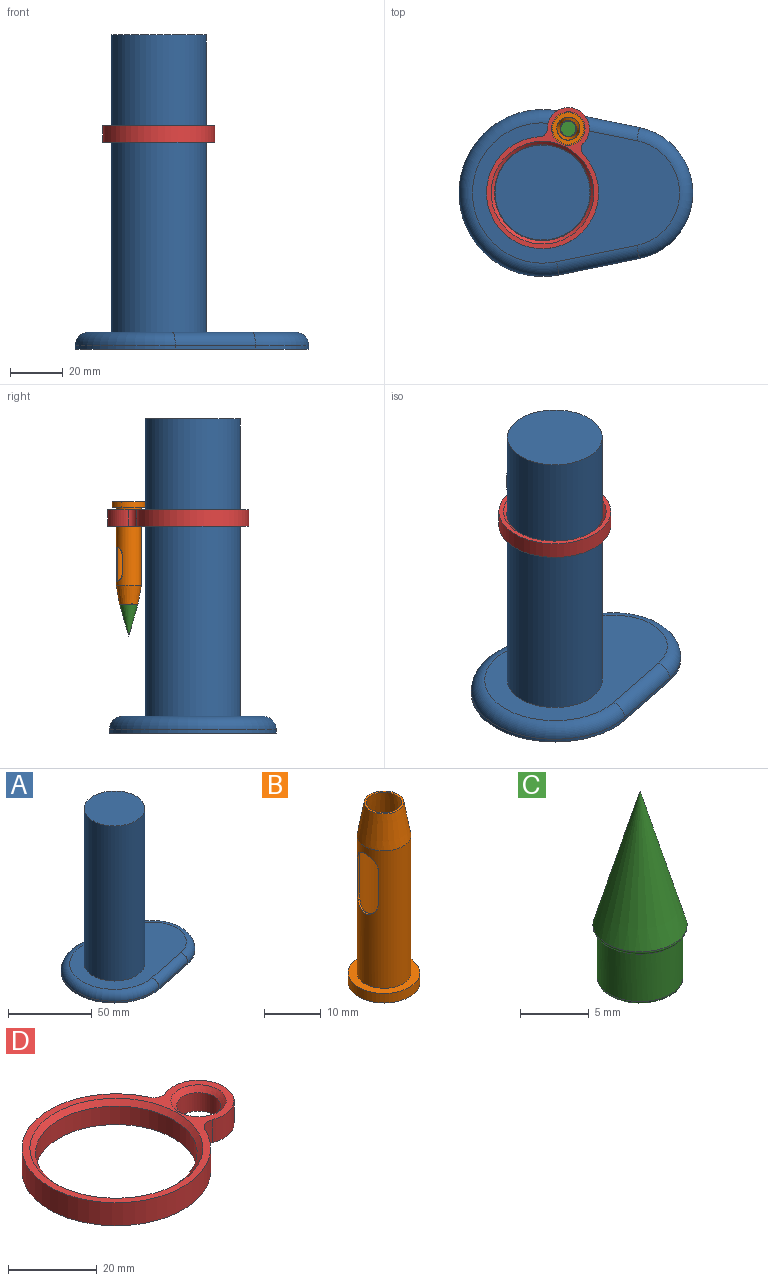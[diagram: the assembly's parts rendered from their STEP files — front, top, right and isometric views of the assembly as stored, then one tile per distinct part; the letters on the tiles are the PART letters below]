
ASSEMBLY  parts=4 mates=3
PART A: 21 faces, bbox 93.6x68.7x119.4 mm
  f0: plane 88.9x63.5mm, normal (0,0,-1), area 600.3mm2, adj f1,f2,f3,f4,f10,f11,f12,f13
  f1: plane 30.48x6.22mm, normal (0.2,0.98,0), area 39.5mm2, adj f0,f2,f4,f8
  f2: cylinder r=31.75mm len=63.5mm, axis (0,0,-1), area 142.9mm2, adj f0,f1,f3,f6
  f3: plane 30.48x6.22mm, normal (0.2,-0.98,0), area 39.5mm2, adj f0,f2,f4,f7
  f4: cylinder r=25.4mm len=49.77mm, axis (0,0,-1), area 88.4mm2, adj f0,f1,f3,f9
  f5: plane 78.74x53.34mm, normal (0,0,1), area 2263.3mm2, adj f6,f7,f8,f9,f19
  f6: torus R=26.67mm, axis (0,0,1), area 845.8mm2, adj f2,f5,f7,f8
  f7: cylinder r=5.08mm len=31.5mm, axis (-0.98,-0.2,0), area 248.2mm2, adj f3,f5,f6,f9
  f8: cylinder r=5.08mm len=31.5mm, axis (0.98,-0.2,0), area 248.2mm2, adj f1,f5,f6,f9
  f9: torus R=20.32mm, axis (0,0,1), area 514.8mm2, adj f4,f5,f7,f8
  f10: plane 30.48x6.22mm, normal (-0.2,-0.98,0), area 39.5mm2, adj f0,f11,f13,f17
  f11: cylinder r=29.21mm len=58.42mm, axis (0,0,-1), area 131.5mm2, adj f0,f10,f12,f15
  f12: plane 30.48x6.22mm, normal (-0.2,0.98,0), area 39.5mm2, adj f0,f11,f13,f16
  f13: cylinder r=22.86mm len=44.8mm, axis (0,0,-1), area 79.5mm2, adj f0,f10,f12,f18
  f14: plane 78.74x53.34mm, normal (0,0,-1), area 3287.7mm2, adj f15,f16,f17,f18
  f15: torus R=26.67mm, axis (0,0,1), area 400mm2, adj f11,f14,f16,f17
  f16: cylinder r=2.54mm len=30.99mm, axis (-0.98,-0.2,0), area 124.1mm2, adj f12,f14,f15,f18
  f17: cylinder r=2.54mm len=30.99mm, axis (0.98,-0.2,0), area 124.1mm2, adj f10,f14,f15,f18
  f18: torus R=20.32mm, axis (0,0,1), area 239.7mm2, adj f13,f14,f16,f17
  f19: cylinder r=18.06mm len=113.03mm, axis (0,0,-1), area 12824.4mm2, adj f5,f20
  f20: plane 36.12x36.12mm, normal (0,0,1), area 1024.4mm2, adj f19
PART B: 20 faces, bbox 12.7x12.7x38.9 mm
  f0: cylinder r=4.76mm len=29.72mm, axis (0,0,-1), area 763.6mm2, adj f3,f5,f11,f12,f13,f14,f15,f16
  f1: cylinder r=4.38mm len=30.07mm, axis (0,0,-1), area 700.7mm2, adj f8,f10,f11,f12,f13,f14,f15,f16
  f2: cylinder r=6.35mm len=12.7mm, axis (0,0,-1), area 82.1mm2, adj f3,f4
  f3: plane 12.7x12.7mm, normal (0,0,1), area 55.4mm2, adj f0,f2
  f4: plane 12.7x12.7mm, normal (0,0,-1), area 66.4mm2, adj f2,f19
  f5: cone r=4.76mm half-angle=10deg, axis (0,0,-1), area 187.6mm2, adj f0,f6
  f6: plane 7.02x7.02mm, normal (0,0,1), area 8.1mm2, adj f5,f10
  f7: cylinder r=5.97mm len=11.94mm, axis (0,0,-1), area 48.6mm2, adj f8,f9
  f8: plane 11.94x11.94mm, normal (0,0,-1), area 51.6mm2, adj f1,f7
  f9: plane 11.94x11.94mm, normal (0,0,1), area 51.6mm2, adj f7,f19
  f10: cone r=4.39mm half-angle=10deg, axis (0,0,-1), area 171mm2, adj f1,f6
  f11: plane 7.8x0.46mm, normal (0,-1,0), area 3.6mm2, adj f0,f1,f12,f14
  f12: cylinder r=2.54mm len=5.08mm, axis (-1,0,0), area 3.3mm2, adj f0,f1,f11,f13
  f13: plane 7.8x0.46mm, normal (0,1,0), area 3.6mm2, adj f0,f1,f12,f14
  f14: cylinder r=2.54mm len=5.08mm, axis (-1,0,0), area 3.3mm2, adj f0,f1,f11,f13
  f15: cylinder r=2.54mm len=5.08mm, axis (-1,0,0), area 3.3mm2, adj f0,f1,f16,f18
  f16: plane 7.8x0.46mm, normal (0,1,0), area 3.6mm2, adj f0,f1,f15,f17
  f17: cylinder r=2.54mm len=5.08mm, axis (-1,0,0), area 3.3mm2, adj f0,f1,f16,f18
  f18: plane 7.8x0.46mm, normal (0,-1,0), area 3.6mm2, adj f0,f1,f15,f17
  f19: cylinder r=4.38mm len=8.76mm, axis (0,0,-1), area 10.5mm2, adj f4,f9
PART C: 6 faces, bbox 7.4x7.4x16.8 mm
  f0: cone r=3.51mm half-angle=16deg, axis (0,0,-1), area 133mm2, adj f5
  f1: plane 6.34x6.34mm, normal (0,0,-1), area 1mm2, adj f2,f5
  f2: cylinder r=3.12mm len=6.24mm, axis (0,0,1), area 84.7mm2, adj f1,f4
  f3: plane 5.74x5.74mm, normal (0,0,-1), area 25.8mm2, adj f4
  f4: torus R=2.87mm, axis (0,0,-1), area 7.6mm2, adj f2,f3
  f5: torus R=3.17mm, axis (0,0,1), area 9.9mm2, adj f0,f1
PART D: 10 faces, bbox 55.6x42.6x6.4 mm
  f0: cylinder r=3.05mm len=6.35mm, axis (0,0,-1), area 29.5mm2, adj f1,f4,f6,f7
  f1: cylinder r=8.01mm len=16.02mm, axis (0,0,-1), area 199.1mm2, adj f0,f2,f6,f7
  f2: cylinder r=3.05mm len=6.35mm, axis (0,0,-1), area 29.5mm2, adj f1,f4,f6,f7
  f3: cylinder r=18.26mm len=36.51mm, axis (0,0,-1), area 582.7mm2, adj f7,f9
  f4: cylinder r=21.3mm len=42.61mm, axis (0,0,-1), area 732.6mm2, adj f0,f2,f6,f7
  f5: cylinder r=4.96mm len=9.92mm, axis (0,0,-1), area 158.3mm2, adj f7,f8
  f6: plane 55.58x42.61mm, normal (0,0,1), area 289.5mm2, adj f0,f1,f2,f4,f8,f9
  f7: plane 55.58x42.61mm, normal (0,0,-1), area 484.9mm2, adj f0,f1,f2,f3,f4,f5
  f8: cone r=4.96mm half-angle=45deg, axis (0,0,1), area 63.1mm2, adj f5,f6
  f9: cone r=18.26mm half-angle=45deg, axis (0,0,1), area 213.2mm2, adj f3,f6
PLACE A t=(-36.45,17.25,-16.63)mm fixed
PLACE B rot(axis=(0.84,-0.54,0),180deg) t=(-26.64,41.62,71.24)mm
PLACE C rot(axis=(0.84,-0.54,0),180deg) t=(-26.64,41.62,71.34)mm
PLACE D rot(axis=(0,0,1),68.1deg) t=(-36.45,17.25,61.94)mm
MATE cylindrical D.f1 <-> B.f0  axis (0,0,1) through (-26.64,41.62,67.02)mm
MATE fastened C.f0 <-> B.f0  axis (0,0,-1) through (-26.64,41.62,32.35)mm
MATE cylindrical D.f3 <-> A.f19  axis (0,0,1) through (-36.45,17.25,67.02)mm
